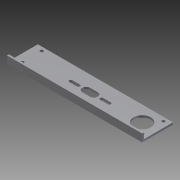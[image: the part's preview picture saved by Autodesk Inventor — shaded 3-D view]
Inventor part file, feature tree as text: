
AUTODESK INVENTOR PART (.ipt)
format: ipt  version: 2012 (Build 160160000, 160)  size: 111,104 bytes
history: native  units: in
note: dims shown in document units (in); Inventor stores cm internally (conversion verified against a paired STEP export)
features: other x3, sketch x2, extrude x1
ambient origin geometry x8: Origin, YZ Plane, XZ Plane, XY Plane, X Axis, Y Axis, Z Axis, Center Point
bodies: Solid1 (feature_tree)
feature tree (6):
  other  "8 ball bottom 1 by 2 L short.ipt"
  extrude  "Extrusion1"  Depth=0.1in
  other  "Solid1::8 ball bottom 1 by 2 L short.ipt"
  sketch  "Sketch1"  dims[d0=0.3937in d1=0.1in]
  sketch  "Sketch2"  dims[d2=0.5in d3=0.25in d4=0.5in d5=1.0in d6=2.125in d7=0.7874in d9=2.0in d10=0.3937in d12=1.0in d14=1.0in d15=0.0in]
  other  "TaggingFeature1"
